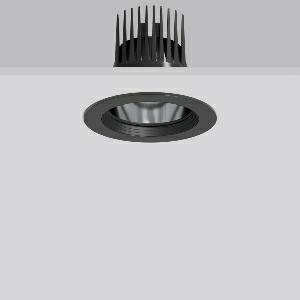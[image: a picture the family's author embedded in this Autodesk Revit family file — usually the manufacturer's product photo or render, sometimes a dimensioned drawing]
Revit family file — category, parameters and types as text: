
# Revit family: heledon_maxi_e_901763_003_3_76_16d3
name_source: partatom
category: Lighting Fixtures
units: mm (PartAtom-declared; Revit-internal decimal feet)

## family parameters
Cut with Voids When Loaded = No
Host = Face
Light Source = No
Part Type = Normal
Room Calculation Point = No
Round Connector Dimension = Use Diameter
Shared = No

## types (1)
- HELEDON maxi E (1 x LED Modul 935, 4250 lm, 3500)
    Apparent Load = 35 VA
    Approval mark = CE
    CIE Flux Codes = 100 100 100 100 100
    Color Rendering = 92
    Color Temperature = 3500
    Default Elevation = 1800 mm
    Description = Series: HELEDON maxi
Round recessed downlight. Housing: die-cast aluminium, powder-coated. Black plastic ring and recessed LED to prevent glare from the side. Optical assembly with reflector made of MIRO-Silver with 98% total light reflection for outstanding efficiency - can be changed without tools. Best colour rendering index Ra>90. Suitable for Recessed ceiling mounting. Installation without tools thanks to spring fastening system. Including separate LED converter with connecting cable 600 mm.High quality converter without flickering and stroboscopic effect. Through-wiring box (5 pole) available as accessory. The following accessories can be mounted without use of tools: interchangeable lenses, decorative glasses, honeycomb louvre, clear and frosted diffusers, white interchangeable plastic ring. 
Colour: deep black, matt (RAL 9005)
Diameter: 162 mm
Height: 3 mm
Cut-out diameter: 152 mm
Recess height: 200 mm
Luminaire: recess height: 135 mm
Lamp: LED
Socket: without socket
Colour temperature: 3500K
Colour rendering index (CRI): 92
System power: 35 W
Rated luminous flux: 4250 lm
Luminous efficiency: 121 lm/W
Control gear: Converter, dimmable, DALI
Protection class: II
Type of protection: IP 20
    Height = 0 mm  [stored 0 ft]
    Lamp = 1 x LED Modul 935
    Lamp Light Flux = 4250 lm
    Lamp count = 1
    Length = 162 mm
    Lifetime = 50000 h
    Luminous efficacy = 121 lm/W
    Manufacturer = RZB
    ModVariant = No
    Model = 901763.003.3.76
    Mounting Place = Ceiling
    Mounting Type = Recessed
    Number of Poles = 1
    OnlyDefault = Yes
    Power Factor = 1
    Product Name = HELEDON maxi E
    Product group = Recessed downlights
    ProductGroupID = 402
    Protection Class = Protection class II
    Protection Degree = IP 20
    RLX_Detail_Level = 1
    RLX_Emergency_Light_Flux = 0 lm
    RLX_Emergency_Type = 0
    RLX_Emergency_Type_DB = No
    RlxData = <blob elided: 120161 chars, md5=7435083b>
    Socket = socket
    Standby Power = 0 W
    System Light Flux = 4250 lm
    System Power = 35 W
    Type Comments = Product without accessories
    Type Image = 901662.003.jpg
    URL = http://relux.com
    VarID = ---
    Voltage = 230 V
    Voltage Range = 220-240 V
    Weight = 0.00 kg
    Width = 0 mm  [stored 0 ft]

note: [stored X ft] marks values corroborated as IEEE doubles in the binary element streams (Revit-internal decimal feet)

## geometry (parser evidence)
native form markers: Blend x4, Sweep x10
no freeform markers — native parametric forms only
